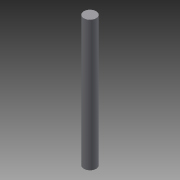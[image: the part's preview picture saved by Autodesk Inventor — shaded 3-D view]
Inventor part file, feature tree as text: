
AUTODESK INVENTOR PART (.ipt)
format: ipt  version: 2014 (Build 180170000, 170)  size: 62,976 bytes
history: native  units: in
note: dims shown in document units (in); Inventor stores cm internally (conversion verified against a paired STEP export)
features: extrude x1, sketch x1
ambient origin geometry x8: Origin, YZ Plane, XZ Plane, XY Plane, X Axis, Y Axis, Z Axis, Center Point
bodies: Solid1 (feature_tree)
feature tree (2):
  extrude  "Extrusion1"  Depth=2.0in TaperAngle=0.0deg
  sketch  "Sketch1"  dims[d0=0.19in d1=2.0in d2=0.0in]
